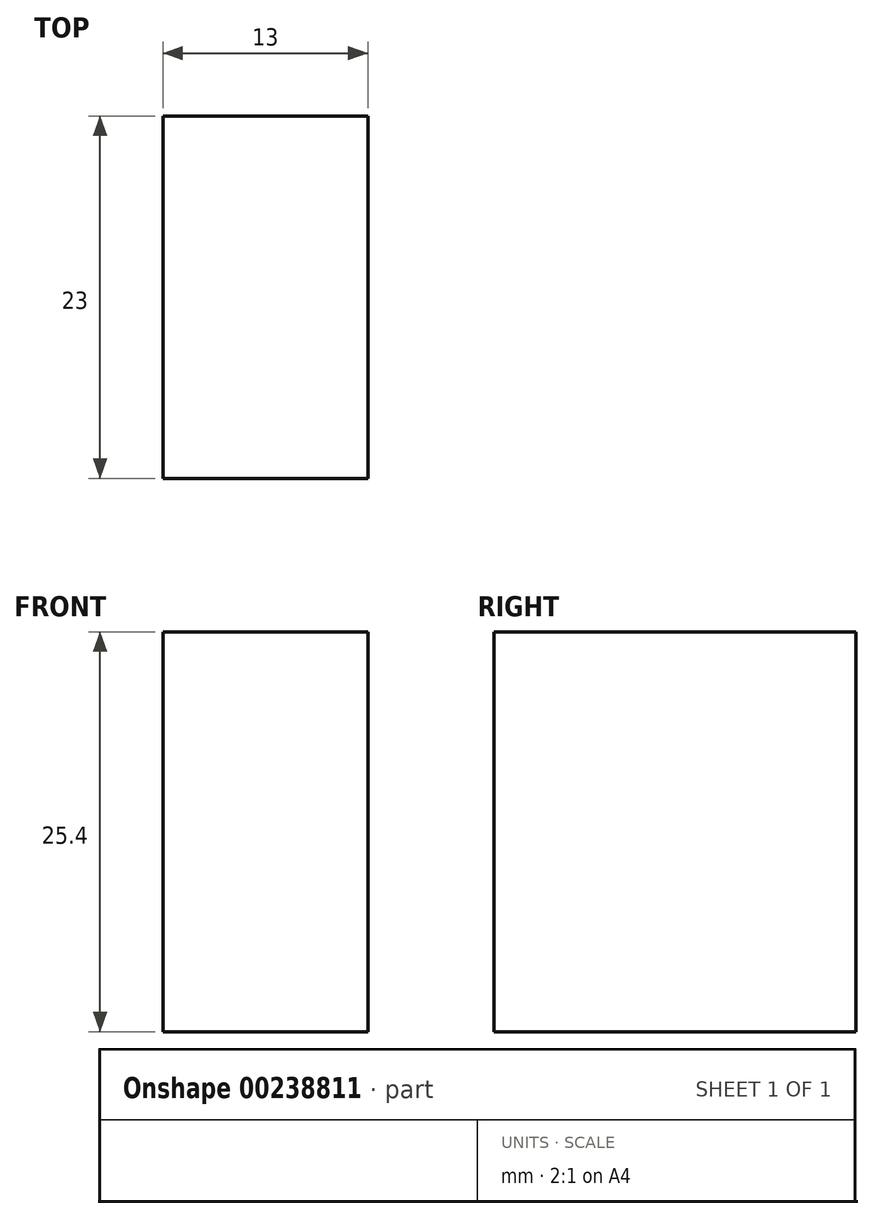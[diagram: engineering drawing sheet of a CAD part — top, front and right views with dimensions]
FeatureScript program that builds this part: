
annotation { "Feature Type Name" : "Feature", "Feature Type Description" : "" }
export const myFeature = defineFeature(function(context is Context, id is Id, definition is map)
    precondition{}
    {
        {
            var Q0;
            Q0=qCreatedBy(makeId("Top.planeOp"),FACE);
            var sketch = newSketch(context, id + "F0", { "sketchPlane" : qUnion([Q0])});
            skLineSegment(sketch, "E0.bottom", {"start": v(0, 0) * mm, "end": v(13, 0) * mm});
            skLineSegment(sketch, "E0.top", {"start": v(0, -23) * mm, "end": v(13, -23) * mm});
            skLineSegment(sketch, "E0.left", {"start": v(0, 0) * mm, "end": v(0, -23) * mm});
            skLineSegment(sketch, "E0.right", {"start": v(13, 0) * mm, "end": v(13, -23) * mm});
            skSolve(sketch);
        }
        {
            var Q0;
            Q0 = qSketchRegion(id + "F0", true);
            extrude(context, id + "F1", {"entities" : qUnion([Q0]), "depth" : 25.4 * mm});
        }
    });
